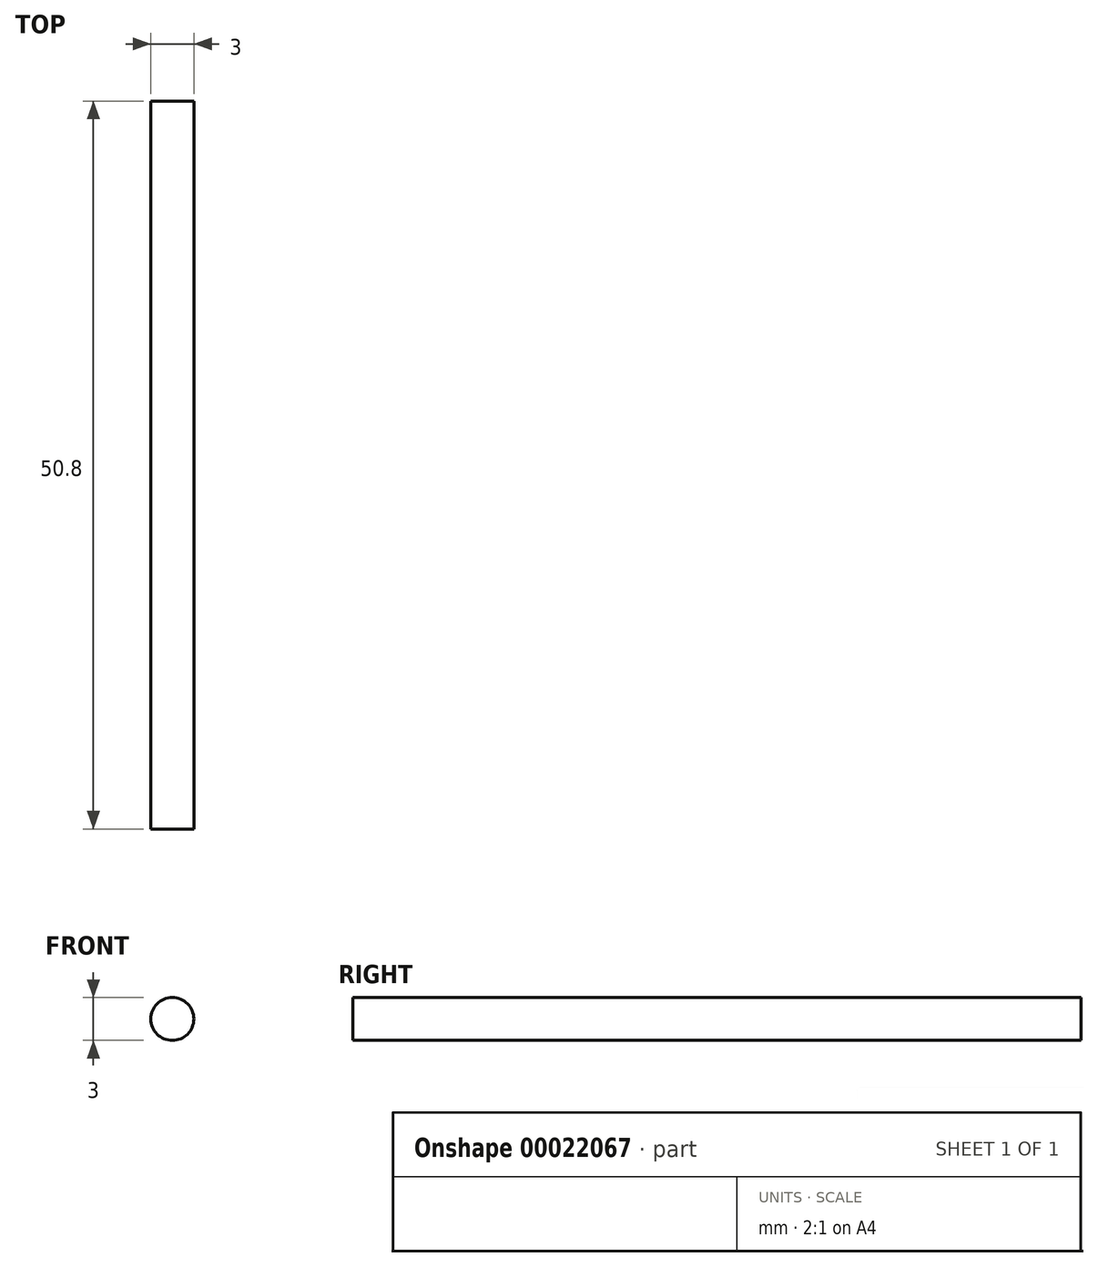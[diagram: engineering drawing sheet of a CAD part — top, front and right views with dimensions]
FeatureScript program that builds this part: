
annotation { "Feature Type Name" : "Feature", "Feature Type Description" : "" }
export const myFeature = defineFeature(function(context is Context, id is Id, definition is map)
    precondition{}
    {
        {
            var Q0;
            Q0=qCreatedBy(makeId("Front.planeOp"),FACE);
            var sketch = newSketch(context, id + "F0", { "sketchPlane" : qUnion([Q0])});
            skCircle(sketch, "E0", {"center": v(-760.59, 7.04) * mm, "radius": 1.5 * mm});
            skSolve(sketch);
        }
        {
            var Q0;
            Q0 = qSketchRegion(id + "F0", true);
            extrude(context, id + "F1", {"entities" : qUnion([Q0]), "depth" : 50.8 * mm});
        }
        {
            var Q0;
            Q0=qCreatedBy(makeId("Front.planeOp"),FACE);
            var sketch = newSketch(context, id + "F2", { "sketchPlane" : qUnion([Q0])});
            skCircle(sketch, "E1", {"center": v(-522.6, 6.63) * mm, "radius": 0.88 * mm});
            skSolve(sketch);
        }
        {
            var Q0;
            Q0=makeQuery(id+"F2.imprint","IMPRINT",FACE,{"disambiguationData":[TD([[makeQuery(id+"F2.imprint","IMPRINT",EDGE,{"derivedFrom":sQuery(id+"F2.wireOp",EDGE,"E1")}),1.0]])]});
            extrude(context, id + "F3", {"entities" : qUnion([Q0]), "depth" : 50.8 * mm});
        }
        {
            var Q0;
            Q0=makeQuery(id+"F3.opExtrude","SWEPT_BODY",BODY,{"disambiguationData":[OSD([sQuery(id+"F2.wireOp",EDGE,"E1")])]});
            deleteBodies(context, id + "F4", {"entities" : qUnion([Q0])});
        }
    });
